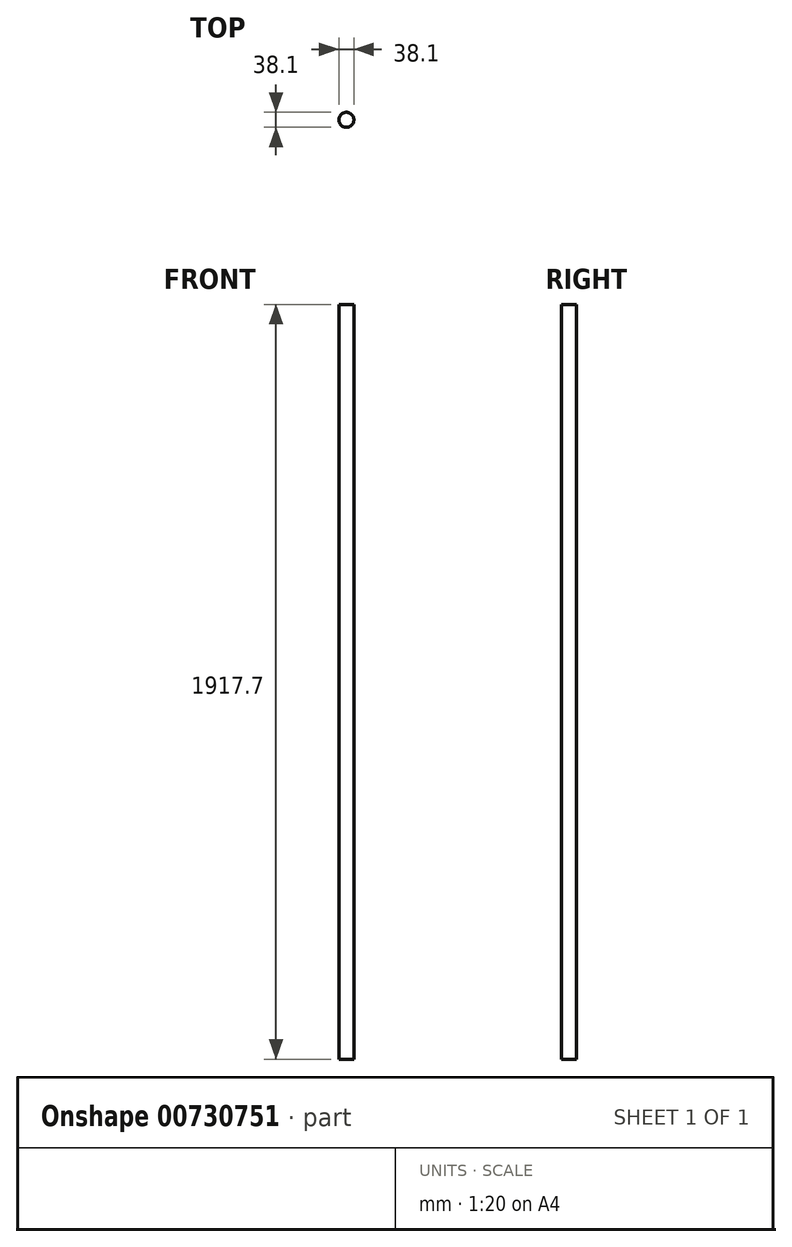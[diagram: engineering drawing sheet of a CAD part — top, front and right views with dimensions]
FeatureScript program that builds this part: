
annotation { "Feature Type Name" : "Feature", "Feature Type Description" : "" }
export const myFeature = defineFeature(function(context is Context, id is Id, definition is map)
    precondition{}
    {
        {
            var Q0;
            Q0=qCreatedBy(makeId("Top.planeOp"),FACE);
            var sketch = newSketch(context, id + "F0", { "sketchPlane" : qUnion([Q0])});
            skCircle(sketch, "E0", {"center": v(0, 0) * mm, "radius": 914.4 * mm, "construction": true});
            skCircle(sketch, "E1", {"center": v(0, 895.35) * mm, "radius": 19.05 * mm});
            skCircle(sketch, "E2.1.0", {"center": v(775.4, 447.68) * mm, "radius": 19.05 * mm, "construction": true});
            skCircle(sketch, "E2.2.0", {"center": v(775.4, -447.67) * mm, "radius": 19.05 * mm, "construction": true});
            skCircle(sketch, "E2.3.0", {"center": v(0, -895.35) * mm, "radius": 19.05 * mm, "construction": true});
            skCircle(sketch, "E2.4.0", {"center": v(-775.4, -447.68) * mm, "radius": 19.05 * mm, "construction": true});
            skCircle(sketch, "E2.5.0", {"center": v(-775.4, 447.67) * mm, "radius": 19.05 * mm, "construction": true});
            skLineSegment(sketch, "E2.anchor1", {"start": v(0, 0) * mm, "end": v(0, 895.35) * mm, "construction": true});
            skLineSegment(sketch, "E2.anchor2", {"start": v(0, 0) * mm, "end": v(-775.4, 447.67) * mm, "construction": true});
            skSolve(sketch);
        }
        {
            var Q0;
            Q0=qCreatedBy(makeId("Front.planeOp"),FACE);
            var sketch = newSketch(context, id + "F1", { "sketchPlane" : qUnion([Q0])});
            skLineSegment(sketch, "E3", {"start": v(0, 0) * mm, "end": v(0, 1828.8) * mm});
            skLineSegment(sketch, "E4", {"start": v(0, 1828.8) * mm, "end": v(452.12, 1828.8) * mm});
            skSolve(sketch);
        }
        {
            var Q0;
            Q0=sQuery(id+"F1.wireOp",EDGE,"E4");
            extrude(context, id + "F2", {"bodyType" : ToolBodyType.SURFACE, "surfaceEntities" : qUnion([Q0]), "depth" : 388.62 * mm, "offsetDistance" : 25.4 * mm});
        }
        {
            var Q0;
            Q0=makeQuery(id+"F0.imprint","IMPRINT",FACE,{"disambiguationData":[TD([[makeQuery(id+"F0.imprint","IMPRINT",EDGE,{"derivedFrom":sQuery(id+"F0.wireOp",EDGE,"E1")}),1.0]])]});
            extrude(context, id + "F3", {"entities" : qUnion([Q0]), "depth" : 1917.7 * mm, "offsetDistance" : 25.4 * mm});
        }
    });
